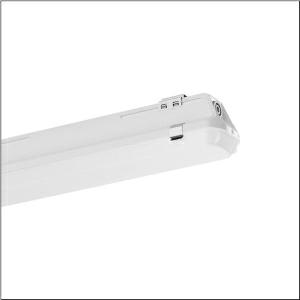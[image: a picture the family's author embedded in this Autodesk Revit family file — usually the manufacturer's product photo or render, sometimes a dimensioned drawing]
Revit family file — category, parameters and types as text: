
# Revit family: monsun_r__11_parking_51fg20dp440h_7f6a
name_source: partatom
category: Lighting Fixtures
units: mm (PartAtom-declared; Revit-internal decimal feet)

## family parameters
Cut with Voids When Loaded = No
Host = Face
Light Source = No
Part Type = Normal
Room Calculation Point = No
Round Connector Dimension = Use Diameter
Shared = No

## types (1)
- --- (1 x LED, 4840 lm, 30.8 W, 4000K)
    Apparent Load = 31 VA
    CIE Flux Codes = 45 75 93 94 100
    Color Rendering = 80
    Color Temperature = 4000K
    Default Elevation = 1800 mm
    Description = Monsun® 11 parking, damp-proof luminaire, chain hanger, primary optical cover: enclosure, of PC, light emission: direct distribution, primary light characteristic: symmetric, installation type: suspended mounting, surface-mounted, horizontal mounting, vertical mounting, LED, rated luminous flux: 4.840lm, luminous efficacy: 157lm/W, light colour: 840, colour temperature: 4000K, control gear: ECG DALI, with terminal, 5-pole, max. 2.5mm², mains connection: 220..240V, AC, 50/60Hz, rated input power: 31W, housing, of glass-fibre reinforced polyester, uncoated, bright grey, incl. chain hanger, length: 1.590mm, width: 90mm, height: 88mm, clip for enclosure, of stainless steel (V2A), ceiling mounting element, of stainless steel (V2A), chain hanger, of stainless steel (V2A), protection rating (complete): IP66, insulation class (complete): insulation class I (protective earthing), certification: CE, ENEC, VDE, UKCA, protection symbol: D, impact resistance: IK08, permissible operating ambient temperature: -25..+40°C, standard: EN 50419, EN 60598-2-1, no direct snow, no direct sun, no direct rain, for indoor or canopied outdoor use, corresponds to IFS (International Featured Standards) requirements for safety and quality in the food industry, contact your sales advisor before using the luminaires in applications with unclear chemical exposure, large temperature fluctuations or condensation-forming humidity, LABS conformity tested according to VDMA 24364:2018-05, packaging unit: 1 piece
    Height = 89 mm
    Lamp = 1 x LED
    Lamp Light Flux = 4840 lm
    Lamp Power = 30.8 W
    Lamp count = 1
    Length = 1590 mm
    Luminous efficacy = 157 lm/W
    Manufacturer = Siteco
    ModVariant = No
    Model = 51FG20DP440H
    Mounting Place = Ceiling
    Mounting Type = Surface mounted
    Number of Poles = 1
    OnlyDefault = Yes
    Power Factor = 1
    Product Name = Monsun® 11 parking
    Product group = damp-proof luminaire
    ProductGroupID = 300
    Protection Class = Protection class I
    Protection Degree = IP 66
    RLX_Detail_Level = 1
    RLX_Emergency_Light_Flux = 0 lm
    RLX_Emergency_Type = 0
    RLX_Emergency_Type_DB = No
    RlxData = <blob elided: 92201 chars, md5=76452249>
    Socket = socket
    Standby Power = 0 W
    System Light Flux = 4840 lm
    System Power = 31 W
    Type Comments = factory setting: luminous flux: 100 % | dim-lin: 254 | 205 mA
    Type Image = l_1319650.jpg
    URL = http://relux.com
    VarID = @adj_173977
    Voltage = 0 V
    Weight = 0.00 kg
    Width = 90 mm

## geometry (parser evidence)
native form markers: Blend x4, Sweep x15
no freeform markers — native parametric forms only
